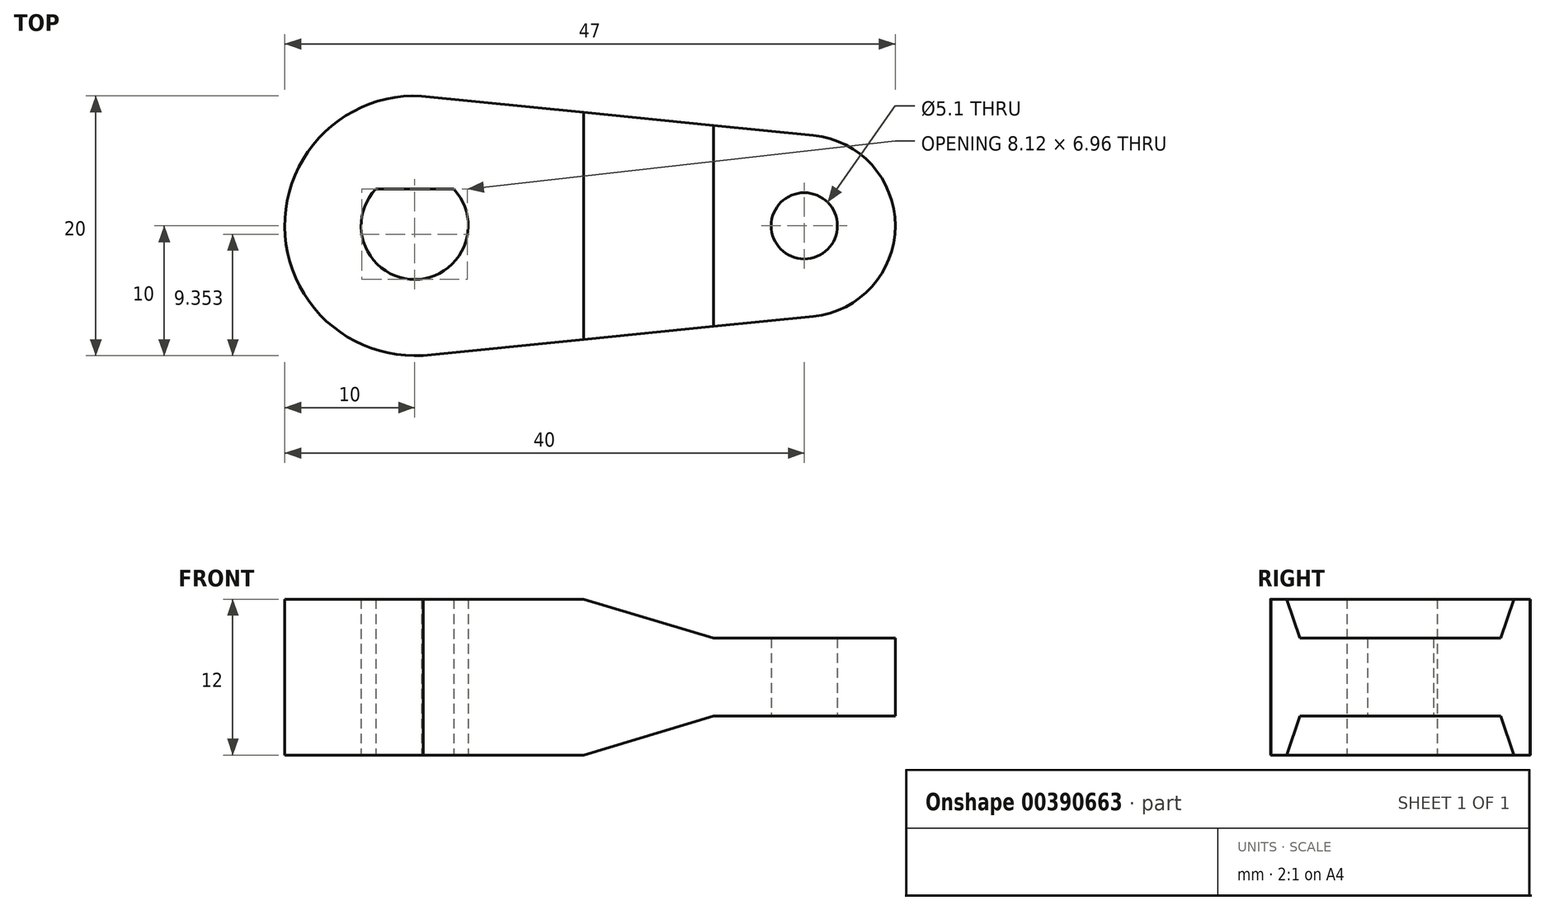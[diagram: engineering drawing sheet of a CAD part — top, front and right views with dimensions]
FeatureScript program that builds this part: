
annotation { "Feature Type Name" : "Feature", "Feature Type Description" : "" }
export const myFeature = defineFeature(function(context is Context, id is Id, definition is map)
    precondition{}
    {
        {
            var Q0;
            Q0=qCreatedBy(makeId("Top.planeOp"),FACE);
            var sketch = newSketch(context, id + "F0", { "sketchPlane" : qUnion([Q0])});
            skCircle(sketch, "E0", {"center": v(0, 0) * mm, "radius": 4.12 * mm});
            skLineSegment(sketch, "E1", {"start": v(-3, 2.83) * mm, "end": v(3, 2.83) * mm});
            skCircle(sketch, "E2", {"center": v(0, 0) * mm, "radius": 10 * mm});
            skCircle(sketch, "E3", {"center": v(30, 0) * mm, "radius": 2.55 * mm});
            skCircle(sketch, "E4", {"center": v(30, 0) * mm, "radius": 7 * mm});
            skLineSegment(sketch, "E5", {"start": v(0.52, 9.99) * mm, "end": v(30.7, 6.97) * mm});
            skLineSegment(sketch, "E6", {"start": v(0.67, -9.98) * mm, "end": v(30.7, -6.97) * mm});
            skLineSegment(sketch, "E7", {"start": v(30, 0) * mm, "end": v(-0.43, 0) * mm, "construction": true});
            skLineSegment(sketch, "E8", {"start": v(23, 7.74) * mm, "end": v(23, -7.74) * mm});
            skSolve(sketch);
        }
        {
            var Q0;
            {var subQ3=sQuery(id+"F0.wireOp",EDGE,"E2");var subQ6=sQuery(id+"F0.wireOp",EDGE,"E5");var subQ7=makeQuery(id+"F0.imprint","INTERSECT",VERTEX,{"disambiguationData":[OD(1.0)],"derivedFrom":[subQ3,subQ6]});Q0=makeQuery(id+"F0.imprint","IMPRINT",FACE,{"disambiguationData":[TD([[makeQuery(id+"F0.imprint","IMPRINT",EDGE,{"disambiguationData":[TD([[subQ7,1.0]])],"derivedFrom":subQ3}),-1.0]])]});}
            var Q1;
            {var subQ7=sQuery(id+"F0.wireOp",EDGE,"E1");var subQ8=sQuery(id+"F0.wireOp",EDGE,"E0");var subQ9=makeQuery(id+"F0.imprint","INTERSECT",VERTEX,{"disambiguationData":[OD(0.0)],"derivedFrom":[subQ8,subQ7]});Q1=makeQuery(id+"F0.imprint","IMPRINT",FACE,{"disambiguationData":[TD([[makeQuery(id+"F0.imprint","IMPRINT",EDGE,{"disambiguationData":[TD([[subQ9,1.0]])],"derivedFrom":subQ8}),-1.0]])]});}
            var Q2;
            {var subQ0=sQuery(id+"F0.wireOp",EDGE,"E1");Q2=makeQuery(id+"F0.imprint","IMPRINT",FACE,{"disambiguationData":[TD([[makeQuery(id+"F0.imprint","IMPRINT",EDGE,{"derivedFrom":subQ0}),1.0]])]});}
            extrude(context, id + "F1", {"entities" : qUnion([Q0, Q1, Q2]), "depth" : 6 * mm});
        }
        {
            var Q0;
            {var subQ0=sQuery(id+"F0.wireOp",EDGE,"E5");var subQ1=sQuery(id+"F0.wireOp",EDGE,"E4");var subQ2=makeQuery(id+"F0.imprint","INTERSECT",VERTEX,{"derivedFrom":[subQ1,subQ0]});Q0=makeQuery(id+"F0.imprint","IMPRINT",FACE,{"disambiguationData":[TD([[makeQuery(id+"F0.imprint","IMPRINT",EDGE,{"disambiguationData":[TD([[subQ2,-1.0]])],"derivedFrom":subQ1}),-1.0]])]});}
            var Q1;
            {var subQ0=sQuery(id+"F0.wireOp",EDGE,"E6");var subQ1=sQuery(id+"F0.wireOp",EDGE,"E4");var subQ2=makeQuery(id+"F0.imprint","INTERSECT",VERTEX,{"derivedFrom":[subQ1,subQ0]});Q1=makeQuery(id+"F0.imprint","IMPRINT",FACE,{"disambiguationData":[TD([[makeQuery(id+"F0.imprint","IMPRINT",EDGE,{"disambiguationData":[TD([[subQ2,1.0]])],"derivedFrom":subQ1}),-1.0]])]});}
            var Q2;
            Q2=makeQuery(id+"F0.imprint","IMPRINT",FACE,{"disambiguationData":[TD([[makeQuery(id+"F0.imprint","IMPRINT",EDGE,{"derivedFrom":sQuery(id+"F0.wireOp",EDGE,"E3")}),-1.0]])]});
            extrude(context, id + "F2", {"entities" : qUnion([Q0, Q1, Q2]), "operationType" : NewBodyOperationType.ADD, "depth" : 3 * mm});
        }
        {
            var Q0;
            Q0=makeQuery(id+"F1.opExtrude","CAP_EDGE",EDGE,{"disambiguationData":[OSD([sQuery(id+"F0.wireOp",EDGE,"E8")])],"isStart":false});
            chamfer(context, id + "F3", {"entities" : qUnion([Q0]), "chamferType" : ChamferType.TWO_OFFSETS, "width1" : 3 * mm, "oppositeDirection" : false, "width2" : 10 * mm, "tangentPropagation" : true});
        }
        {
            var Q0;
            Q0=makeQuery(id+"F1.opExtrude","SWEPT_BODY",BODY,{"disambiguationData":[OSD([sQuery(id+"F0.wireOp",EDGE,"E0"),sQuery(id+"F0.wireOp",EDGE,"E1"),sQuery(id+"F0.wireOp",EDGE,"E2"),sQuery(id+"F0.wireOp",EDGE,"E5"),sQuery(id+"F0.wireOp",EDGE,"E6"),sQuery(id+"F0.wireOp",EDGE,"E8")])]});
            var Q1;
            Q1=qCreatedBy(makeId("Top.planeOp"),FACE);
            mirror(context, id + "F4", {"operationType" : NewBodyOperationType.ADD, "entities" : qUnion([Q0]), "mirrorPlane" : qUnion([Q1])});
        }
    });
